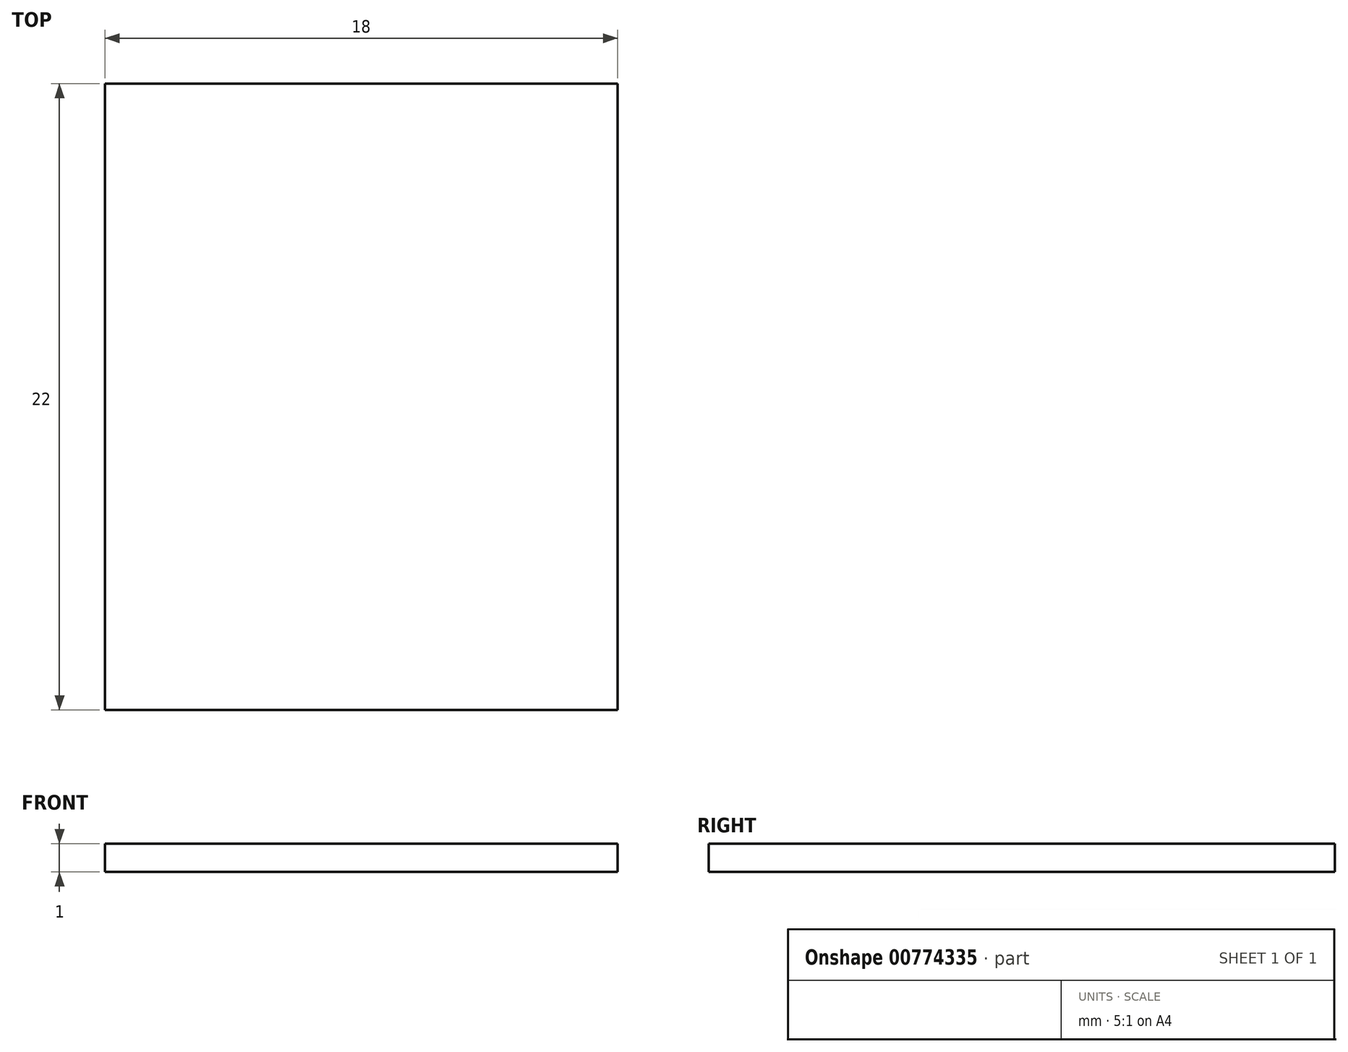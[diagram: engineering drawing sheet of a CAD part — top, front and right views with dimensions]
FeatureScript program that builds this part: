
annotation { "Feature Type Name" : "Feature", "Feature Type Description" : "" }
export const myFeature = defineFeature(function(context is Context, id is Id, definition is map)
    precondition{}
    {
        {
            var Q0;
            Q0=qCreatedBy(makeId("Top.planeOp"),FACE);
            var sketch = newSketch(context, id + "F0", { "sketchPlane" : qUnion([Q0])});
            skLineSegment(sketch, "E0.bottom", {"start": v(-9, 10) * mm, "end": v(9, 10) * mm});
            skLineSegment(sketch, "E0.top", {"start": v(-9, -12) * mm, "end": v(9, -12) * mm});
            skLineSegment(sketch, "E0.left", {"start": v(-9, 10) * mm, "end": v(-9, -12) * mm});
            skLineSegment(sketch, "E0.right", {"start": v(9, 10) * mm, "end": v(9, -12) * mm});
            skSolve(sketch);
        }
        {
            var Q0;
            Q0 = qSketchRegion(id + "F0", true);
            extrude(context, id + "F1", {"entities" : qUnion([Q0]), "depth" : 1 * mm, "offsetDistance" : 25 * mm});
        }
    });
